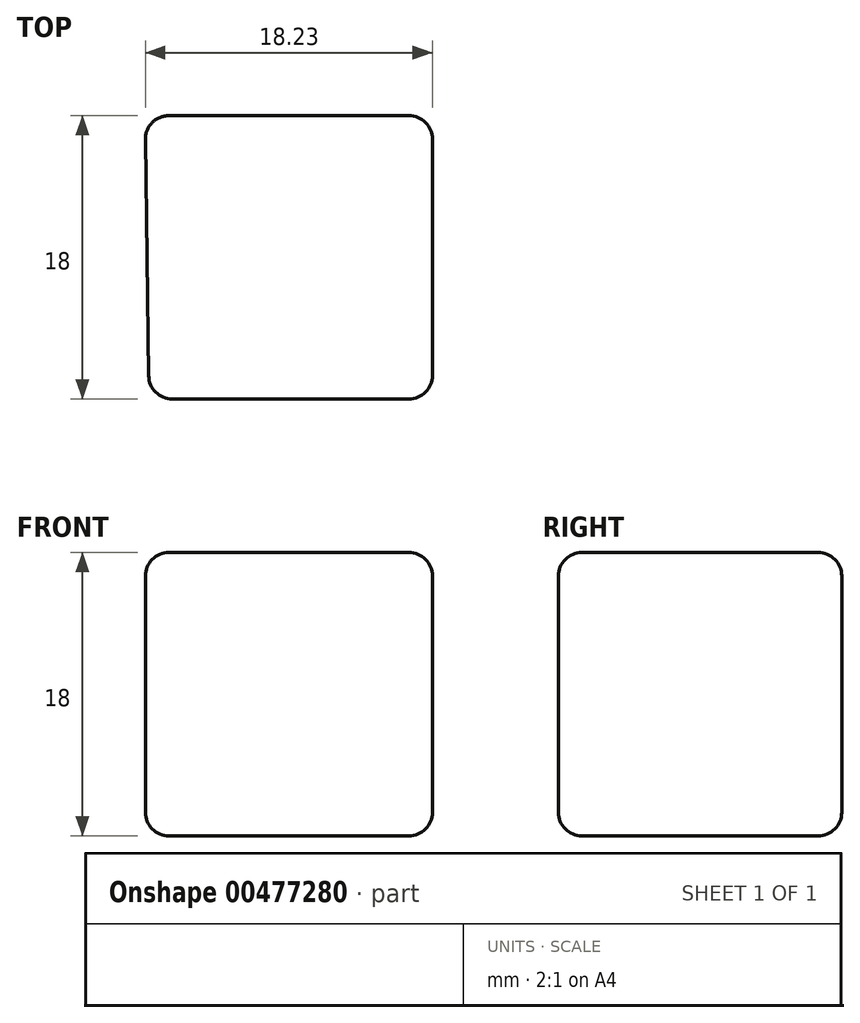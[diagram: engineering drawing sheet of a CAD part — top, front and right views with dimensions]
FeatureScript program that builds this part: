
annotation { "Feature Type Name" : "Feature", "Feature Type Description" : "" }
export const myFeature = defineFeature(function(context is Context, id is Id, definition is map)
    precondition{}
    {
        {
            var Q0;
            Q0=qCreatedBy(makeId("Top.planeOp"),FACE);
            var sketch = newSketch(context, id + "F0", { "sketchPlane" : qUnion([Q0])});
            skLineSegment(sketch, "E0", {"start": v(-18.25, 0) * mm, "end": v(0, 0) * mm});
            skLineSegment(sketch, "E1", {"start": v(0, 0) * mm, "end": v(0, -18) * mm});
            skLineSegment(sketch, "E2", {"start": v(0, -18) * mm, "end": v(-18, -18) * mm});
            skLineSegment(sketch, "E3", {"start": v(-18, -18) * mm, "end": v(-18.25, 0) * mm});
            skSolve(sketch);
        }
        {
            var Q0;
            Q0=makeQuery(id+"F0.imprint","IMPRINT",FACE,{"disambiguationData":[TD([[makeQuery(id+"F0.imprint","IMPRINT",EDGE,{"derivedFrom":sQuery(id+"F0.wireOp",EDGE,"E0")}),-1.0]])]});
            extrude(context, id + "F1", {"entities" : qUnion([Q0]), "depth" : 18 * mm});
        }
        {
            var Q0;
            Q0=makeQuery(id+"F1.opExtrude","CAP_EDGE",EDGE,{"disambiguationData":[OSD([sQuery(id+"F0.wireOp",EDGE,"E2")])],"isStart":false});
            var Q1;
            Q1=makeQuery(id+"F1.opExtrude","SWEPT_EDGE",EDGE,{"disambiguationData":[OSD([sQuery(id+"F0.wireOp",EDGE,"E1"),sQuery(id+"F0.wireOp",EDGE,"E2")])]});
            var Q2;
            Q2=makeQuery(id+"F1.opExtrude","SWEPT_EDGE",EDGE,{"disambiguationData":[OSD([sQuery(id+"F0.wireOp",EDGE,"E2"),sQuery(id+"F0.wireOp",EDGE,"E3")])]});
            var Q3;
            Q3=makeQuery(id+"F1.opExtrude","CAP_EDGE",EDGE,{"disambiguationData":[OSD([sQuery(id+"F0.wireOp",EDGE,"E2")])],"isStart":true});
            var Q4;
            Q4=makeQuery(id+"F1.opExtrude","CAP_EDGE",EDGE,{"disambiguationData":[OSD([sQuery(id+"F0.wireOp",EDGE,"E1")])],"isStart":false});
            var Q5;
            Q5=makeQuery(id+"F1.opExtrude","SWEPT_EDGE",EDGE,{"disambiguationData":[OSD([sQuery(id+"F0.wireOp",EDGE,"E0"),sQuery(id+"F0.wireOp",EDGE,"E1")])]});
            var Q6;
            Q6=makeQuery(id+"F1.opExtrude","CAP_EDGE",EDGE,{"disambiguationData":[OSD([sQuery(id+"F0.wireOp",EDGE,"E1")])],"isStart":true});
            var Q7;
            Q7=makeQuery(id+"F1.opExtrude","CAP_EDGE",EDGE,{"disambiguationData":[OSD([sQuery(id+"F0.wireOp",EDGE,"E0")])],"isStart":false});
            var Q8;
            Q8=makeQuery(id+"F1.opExtrude","CAP_EDGE",EDGE,{"disambiguationData":[OSD([sQuery(id+"F0.wireOp",EDGE,"E0")])],"isStart":true});
            var Q9;
            Q9=makeQuery(id+"F1.opExtrude","CAP_EDGE",EDGE,{"disambiguationData":[OSD([sQuery(id+"F0.wireOp",EDGE,"E3")])],"isStart":true});
            var Q10;
            Q10=makeQuery(id+"F1.opExtrude","CAP_EDGE",EDGE,{"disambiguationData":[OSD([sQuery(id+"F0.wireOp",EDGE,"E3")])],"isStart":false});
            var Q11;
            Q11=makeQuery(id+"F1.opExtrude","SWEPT_EDGE",EDGE,{"disambiguationData":[OSD([sQuery(id+"F0.wireOp",EDGE,"E0"),sQuery(id+"F0.wireOp",EDGE,"E3")])]});
            fillet(context, id + "F2", {"entities" : qUnion([Q0, Q1, Q2, Q3, Q4, Q5, Q6, Q7, Q8, Q9, Q10, Q11]), "radius" : 1.5 * mm, "tangentPropagation" : true, "allowEdgeOverflow" : false});
        }
    });
